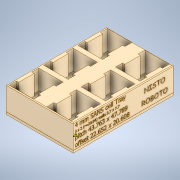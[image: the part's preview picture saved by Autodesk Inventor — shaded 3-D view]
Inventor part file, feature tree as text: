
AUTODESK INVENTOR PART (.ipt)
format: ipt  version: 2020 (Build 240168000, 168)  size: 2,661,376 bytes
history: native  units: in
note: dims shown in document units (in); Inventor stores cm internally (conversion verified against a paired STEP export)
features: extrude x3, sketch x3, fillet x1, emboss x1, pattern_linear x1
ambient origin geometry x8: Origin, YZ Plane, XZ Plane, XY Plane, X Axis, Y Axis, Z Axis, Center Point
bodies: Solid1 (feature_tree)
feature tree (9):
  extrude  "Extrusion1"  TaperAngle=45.0deg  [1 undecoded]
  extrude  "Extrusion2"  TaperAngle=225.0deg  [1 undecoded]
  extrude  "Extrusion3"  Depth=0.0394in TaperAngle=0.0deg
  fillet  "Fillet1"  Radius=0.2112in
  emboss  "Emboss2"
  pattern_linear  "Rectangular Pattern2"  Spacing1=0.0483in  [1 undecoded]
  sketch  "Sketch1"  dims[d3=0.0in d5=45.0deg]
  sketch  "Sketch2"  dims[d6=0.0079in d7=225.0deg]
  sketch  "Sketch5"  dims[d9=0.0in d48=0.0394in d49=0.0in d50=0.2112in d51=0.0483in d52=1.0in d53=1.478in d54=0.11in d55=0.35in d56=0.11in d57=0.35in d58=0.11in d59=0.35in d60=0.11in d61=0.35in d62=1.0in d63=0.0in d64=1.1811in d66=1.7229in d67=0.7874in d69=1.8815in d65=0.0344in]
note: 3 required parameter values undecoded (feature->parameter linkage not recoverable at this tier; creation-order binding heuristic only, values carry confidence <= 0.55)
